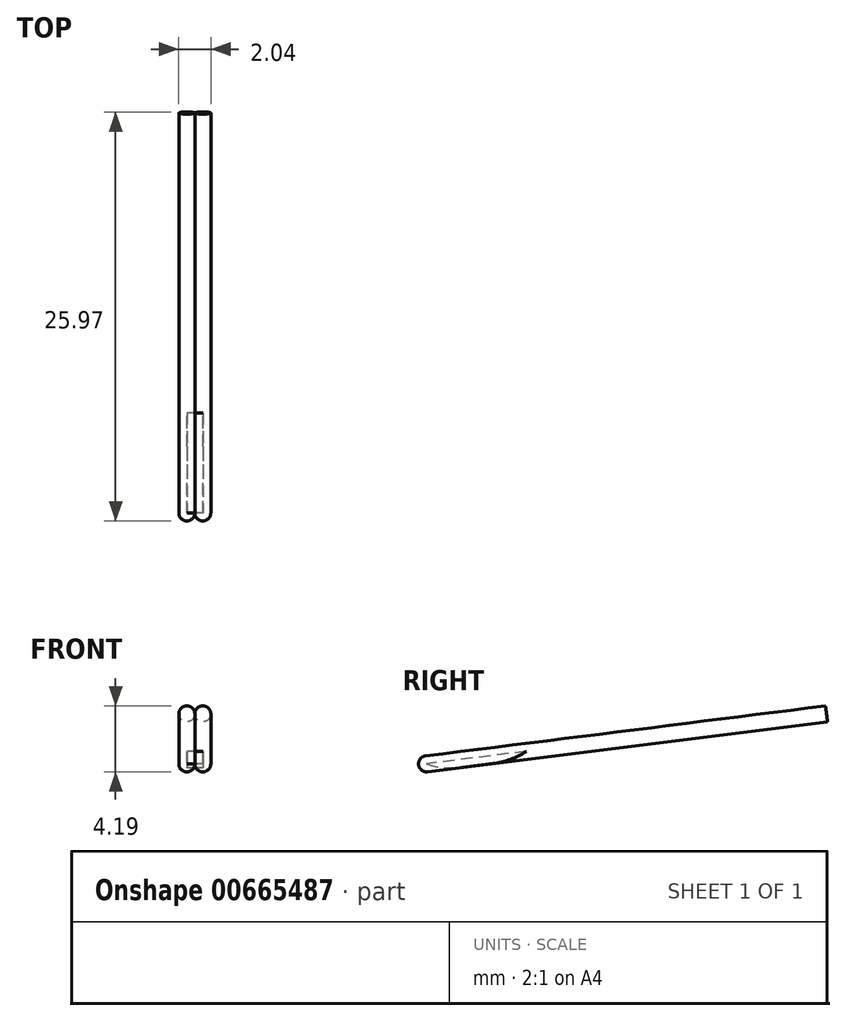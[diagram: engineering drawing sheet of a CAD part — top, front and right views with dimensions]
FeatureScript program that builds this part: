
annotation { "Feature Type Name" : "Feature", "Feature Type Description" : "" }
export const myFeature = defineFeature(function(context is Context, id is Id, definition is map)
    precondition{}
    {
        {
            var Q0;
            Q0=qCreatedBy(makeId("Front.planeOp"),FACE);
            var sketch = newSketch(context, id + "F0", { "sketchPlane" : qUnion([Q0])});
            skCircle(sketch, "E0", {"center": v(0, 0) * mm, "radius": 6.35 * mm});
            skSolve(sketch);
        }
        {
            var Q0;
            Q0=qCreatedBy(makeId("Front.planeOp"),FACE);
            cPlane(context, id + "F1", {"entities" : qUnion([Q0]), "cplaneType" : CPlaneType.OFFSET, "offset" : 25.4 * mm, "width" : 152.4 * mm, "height" : 152.4 * mm});
        }
        {
            var Q0;
            Q0=qCreatedBy(makeId("Front.planeOp"),FACE);
            cPlane(context, id + "F2", {"entities" : qUnion([Q0]), "cplaneType" : CPlaneType.OFFSET, "offset" : 19.05 * mm, "width" : 152.4 * mm, "height" : 152.4 * mm});
        }
        {
            var Q0;
            Q0=qCreatedBy(makeId("Right.planeOp"),FACE);
            cPlane(context, id + "F3", {"entities" : qUnion([Q0]), "cplaneType" : CPlaneType.OFFSET, "offset" : 0.5 * mm, "width" : 152.4 * mm, "height" : 152.4 * mm});
        }
        {
            var Q0;
            Q0=qCreatedBy(makeId("Right.planeOp"),FACE);
            cPlane(context, id + "F4", {"entities" : qUnion([Q0]), "cplaneType" : CPlaneType.OFFSET, "offset" : 0.5 * mm, "oppositeDirection" : true, "width" : 152.4 * mm, "height" : 152.4 * mm});
        }
        {
            var Q0;
            Q0=qCreatedBy(id+"F3.planeOp",FACE);
            var sketch = newSketch(context, id + "F5", { "sketchPlane" : qUnion([Q0])});
            skLineSegment(sketch, "E1", {"start": v(0, 3.17) * mm, "end": v(-25.4, 0) * mm});
            skLineSegment(sketch, "E2.0", {"start": v(-0.06, 3.68) * mm, "end": v(-25.46, 0.5) * mm});
            skLineSegment(sketch, "E3", {"start": v(-0.06, 3.68) * mm, "end": v(0, 3.17) * mm});
            skLineSegment(sketch, "E4", {"start": v(-25.46, 0.5) * mm, "end": v(-25.4, 0) * mm});
            skSolve(sketch);
        }
        {
            var Q0;
            Q0=qCreatedBy(id+"F4.planeOp",FACE);
            var sketch = newSketch(context, id + "F6", { "sketchPlane" : qUnion([Q0])});
            skLineSegment(sketch, "E5", {"start": v(0, 3.18) * mm, "end": v(-25.4, 0) * mm});
            skLineSegment(sketch, "E6.0", {"start": v(-0.06, 3.68) * mm, "end": v(-25.46, 0.5) * mm});
            skLineSegment(sketch, "E7", {"start": v(-0.06, 3.68) * mm, "end": v(0, 3.18) * mm});
            skLineSegment(sketch, "E8", {"start": v(-25.46, 0.5) * mm, "end": v(-25.4, 0) * mm});
            skSolve(sketch);
        }
        {
            var Q0;
            Q0 = qSketchRegion(id + "F5", true);
            var Q1;
            Q1=sQuery(id+"F5.wireOp",EDGE,"E1");
            revolve(context, id + "F7", {"entities" : qUnion([Q0]), "axis" : qUnion([Q1]), "revolveType" : RevolveType.FULL});
        }
        {
            var Q0;
            Q0 = qSketchRegion(id + "F6", true);
            var Q1;
            Q1=sQuery(id+"F6.wireOp",EDGE,"E5");
            revolve(context, id + "F8", {"operationType" : NewBodyOperationType.ADD, "entities" : qUnion([Q0]), "axis" : qUnion([Q1]), "revolveType" : RevolveType.FULL});
        }
        {
            var Q0;
            Q0=qCreatedBy(id+"F1.planeOp",FACE);
            var sketch = newSketch(context, id + "F9", { "sketchPlane" : qUnion([Q0])});
            skCircle(sketch, "E9", {"center": v(-0.5, 0) * mm, "radius": 0.5 * mm});
            skLineSegment(sketch, "E10", {"start": v(0, 0) * mm, "end": v(-1.02, 0) * mm});
            skSolve(sketch);
        }
        {
            var Q0;
            Q0=qCreatedBy(id+"F1.planeOp",FACE);
            var sketch = newSketch(context, id + "F10", { "sketchPlane" : qUnion([Q0])});
            skCircle(sketch, "E11", {"center": v(0.5, 0) * mm, "radius": 0.5 * mm});
            skLineSegment(sketch, "E12", {"start": v(0, 0) * mm, "end": v(1.02, 0) * mm});
            skSolve(sketch);
        }
        {
            var Q0;
            {var subQ0=sQuery(id+"F9.wireOp",EDGE,"E10");Q0=makeQuery(id+"F9.imprint","IMPRINT",FACE,{"disambiguationData":[TD([[makeQuery(id+"F9.imprint","IMPRINT",EDGE,{"derivedFrom":subQ0}),1.0]])]});}
            var Q1;
            Q1=sQuery(id+"F9.wireOp",EDGE,"E10");
            revolve(context, id + "F11", {"operationType" : NewBodyOperationType.ADD, "entities" : qUnion([Q0]), "axis" : qUnion([Q1]), "revolveType" : RevolveType.FULL});
        }
        {
            var Q0;
            {var subQ0=sQuery(id+"F10.wireOp",EDGE,"E12");Q0=makeQuery(id+"F10.imprint","IMPRINT",FACE,{"disambiguationData":[TD([[makeQuery(id+"F10.imprint","IMPRINT",EDGE,{"derivedFrom":subQ0}),-1.0]])]});}
            var Q1;
            Q1=sQuery(id+"F10.wireOp",EDGE,"E12");
            revolve(context, id + "F12", {"operationType" : NewBodyOperationType.ADD, "entities" : qUnion([Q0]), "axis" : qUnion([Q1]), "revolveType" : RevolveType.FULL});
        }
        {
            var Q0;
            Q0=qCreatedBy(makeId("Right.planeOp"),FACE);
            var sketch = newSketch(context, id + "F13", { "sketchPlane" : qUnion([Q0])});
            skLineSegment(sketch, "E13", {"start": v(0, 3.18) * mm, "end": v(-25.4, 0) * mm});
            skLineSegment(sketch, "E14.0", {"start": v(0.06, 2.67) * mm, "end": v(-25.34, -0.5) * mm});
            skLineSegment(sketch, "E15", {"start": v(-25.4, 0) * mm, "end": v(-25.34, -0.5) * mm});
            skLineSegment(sketch, "E16", {"start": v(0, 3.18) * mm, "end": v(0.06, 2.67) * mm});
            skLineSegment(sketch, "E17", {"start": v(-19.05, 0.8) * mm, "end": v(-19.05, 0.28) * mm});
            skSolve(sketch);
        }
        {
            var Q0;
            {var subQ0=sQuery(id+"F13.wireOp",EDGE,"E15");Q0=makeQuery(id+"F13.imprint","IMPRINT",FACE,{"disambiguationData":[TD([[makeQuery(id+"F13.imprint","IMPRINT",EDGE,{"derivedFrom":subQ0}),1.0]])]});}
            extrude(context, id + "F14", {"entities" : qUnion([Q0]), "depth" : 0.5 * mm, "offsetDistance" : 25.4 * mm, "hasSecondDirection" : true, "secondDirectionOppositeDirection" : true, "secondDirectionDepth" : 0.5 * mm});
        }
        {
            var Q0;
            Q0=makeQuery(id+"F14.opExtrude","SWEPT_EDGE",EDGE,{"disambiguationData":[OSD([sQuery(id+"F13.wireOp",EDGE,"E14.0"),sQuery(id+"F13.wireOp",EDGE,"E15")])]});
            fillet(context, id + "F15", {"entities" : qUnion([Q0]), "radius" : 5.08 * mm, "tangentPropagation" : true, "allowEdgeOverflow" : false});
        }
        {
            var Q0;
            Q0=makeQuery(id+"F14.opExtrude","SWEPT_EDGE",EDGE,{"disambiguationData":[OSD([sQuery(id+"F13.wireOp",EDGE,"E14.0"),sQuery(id+"F13.wireOp",EDGE,"E17")])]});
            fillet(context, id + "F16", {"entities" : qUnion([Q0]), "radius" : 5.08 * mm, "tangentPropagation" : true, "allowEdgeOverflow" : false});
        }
    });
